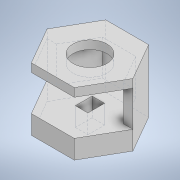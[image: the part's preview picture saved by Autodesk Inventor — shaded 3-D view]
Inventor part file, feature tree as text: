
AUTODESK INVENTOR PART (.ipt)
format: ipt  version: 2021 (Build 250183000, 183)  size: 177,664 bytes
history: native  units: mm
features: extrude x6, sketch x5, projected_geometry x5
ambient origin geometry x8: Origin, YZ Plane, XZ Plane, XY Plane, X Axis, Y Axis, Z Axis, Center Point
bodies: Solid1 (feature_tree)
feature tree (16):
  sketch  "Sketch1"  dims[d0=8.1mm d1=7.25mm]
  extrude  "Extrusion1"  Depth=7.25mm
  extrude  "Extrusion2"  Depth=2.0mm TaperAngle=0.0deg
  extrude  "Extrusion3"  Depth=5.0mm TaperAngle=0.0deg
  extrude  "Extrusion4"  Depth=3.0mm
  extrude  "Extrusion6"  Depth=3.0mm
  extrude  "Extrusion7"  Depth=4.0mm
  sketch  "Sketch2"  dims[d2=3.0mm d3=2.0mm d4=0.0mm]
  projected_geometry  "Projected Loop1"
  projected_geometry  "Projected Loop2"
  sketch  "Sketch3"  dims[d5=8.0mm d6=0.0mm d7=5.0mm d8=0.0mm]
  projected_geometry  "Projected Loop3"
  sketch  "Sketch5"  dims[d9=1.5mm d10=3.0mm]
  projected_geometry  "Projected Loop5"
  sketch  "Sketch6"  dims[d11=2.0mm d12=3.0mm d13=4.0mm d14=4.5mm d15=0.0mm d19=0.75mm d20=10.0mm d21=0.0mm d22=10.0mm d23=0.0mm]
  projected_geometry  "Projected Loop6"
